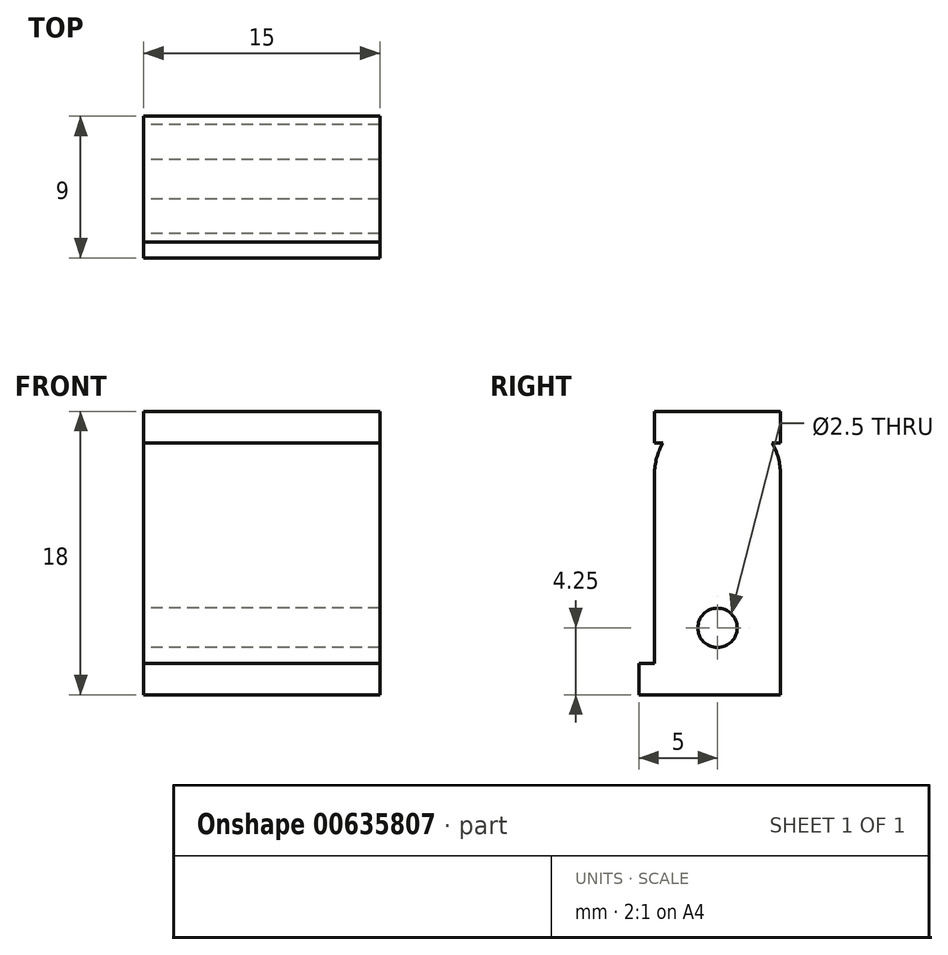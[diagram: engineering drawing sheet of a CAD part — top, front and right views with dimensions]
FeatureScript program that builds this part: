
annotation { "Feature Type Name" : "Feature", "Feature Type Description" : "" }
export const myFeature = defineFeature(function(context is Context, id is Id, definition is map)
    precondition{}
    {
        {
            var Q0;
            Q0=qCreatedBy(makeId("Right.planeOp"),FACE);
            var sketch = newSketch(context, id + "F0", { "sketchPlane" : qUnion([Q0])});
            skLineSegment(sketch, "E0.bottom", {"start": v(-4, -1) * mm, "end": v(-3.46, -1) * mm});
            skLineSegment(sketch, "E0.top", {"start": v(-4, 1) * mm, "end": v(4, 1) * mm});
            skLineSegment(sketch, "E0.left", {"start": v(-4, -1) * mm, "end": v(-4, 1) * mm});
            skLineSegment(sketch, "E0.right", {"start": v(4, -1) * mm, "end": v(4, 1) * mm});
            skPoint(sketch, "E0.middle", {"position": v(0, 0) * mm});
            skArc(sketch, "E1", {"start": v(-3.46, -1) * mm, "mid": v(-3.86, -1.96) * mm, "end": v(-4, -3) * mm});
            skPoint(sketch, "E1.centerSnap0", {"position": v(0, -1) * mm});
            skLineSegment(sketch, "E2.left", {"start": v(4, -3) * mm, "end": v(4, -15) * mm});
            skLineSegment(sketch, "E2.right", {"start": v(-4, -3) * mm, "end": v(-4, -15) * mm});
            skLineSegment(sketch, "E3.bottom", {"start": v(-4, -15) * mm, "end": v(-5, -15) * mm});
            skLineSegment(sketch, "E3.top", {"start": v(4, -17) * mm, "end": v(-5, -17) * mm});
            skLineSegment(sketch, "E3.left", {"start": v(4, -15) * mm, "end": v(4, -17) * mm});
            skLineSegment(sketch, "E3.right", {"start": v(-5, -15) * mm, "end": v(-5, -17) * mm});
            skCircle(sketch, "E4", {"center": v(0, -12.75) * mm, "radius": 1.25 * mm});
            skLineSegment(sketch, "E5.trimOffspring", {"start": v(3.46, -1) * mm, "end": v(4, -1) * mm});
            skArc(sketch, "E6.trimOffspring", {"start": v(4, -3) * mm, "mid": v(3.86, -1.96) * mm, "end": v(3.46, -1) * mm});
            skSolve(sketch);
        }
        {
            var Q0;
            Q0 = qSketchRegion(id + "F0", true);
            extrude(context, id + "F1", {"entities" : qUnion([Q0]), "endBound" : BoundingType.SYMMETRIC, "depth" : 15 * mm, "offsetDistance" : 25.4 * mm});
        }
    });
